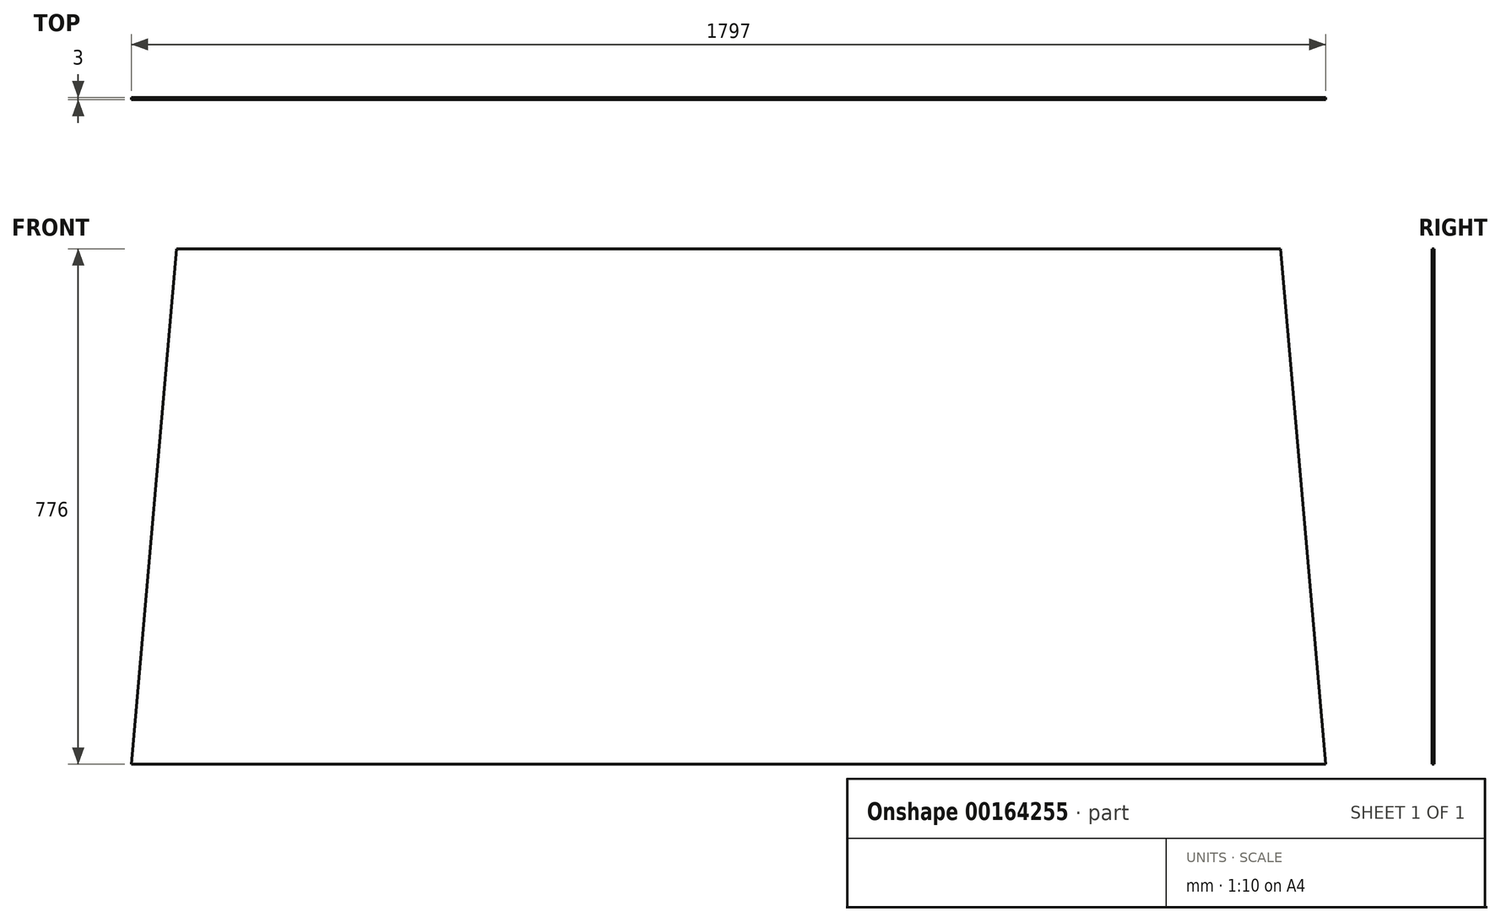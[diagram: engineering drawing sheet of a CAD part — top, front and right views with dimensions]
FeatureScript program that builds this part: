
annotation { "Feature Type Name" : "Feature", "Feature Type Description" : "" }
export const myFeature = defineFeature(function(context is Context, id is Id, definition is map)
    precondition{}
    {
        {
            var Q0;
            Q0=qCreatedBy(makeId("Front.planeOp"),FACE);
            var sketch = newSketch(context, id + "F0", { "sketchPlane" : qUnion([Q0])});
            skLineSegment(sketch, "E0", {"start": v(2085.98, 172.84) * mm, "end": v(2018.1, 948.84) * mm});
            skLineSegment(sketch, "E1", {"start": v(2018.1, 948.84) * mm, "end": v(356.88, 948.84) * mm});
            skLineSegment(sketch, "E2", {"start": v(356.88, 948.84) * mm, "end": v(288.98, 172.84) * mm});
            skLineSegment(sketch, "E3", {"start": v(288.98, 172.84) * mm, "end": v(2085.98, 172.84) * mm});
            skSolve(sketch);
        }
        {
            var Q0;
            Q0 = qSketchRegion(id + "F0", true);
            extrude(context, id + "F1", {"entities" : qUnion([Q0]), "depth" : 3 * mm});
        }
    });
